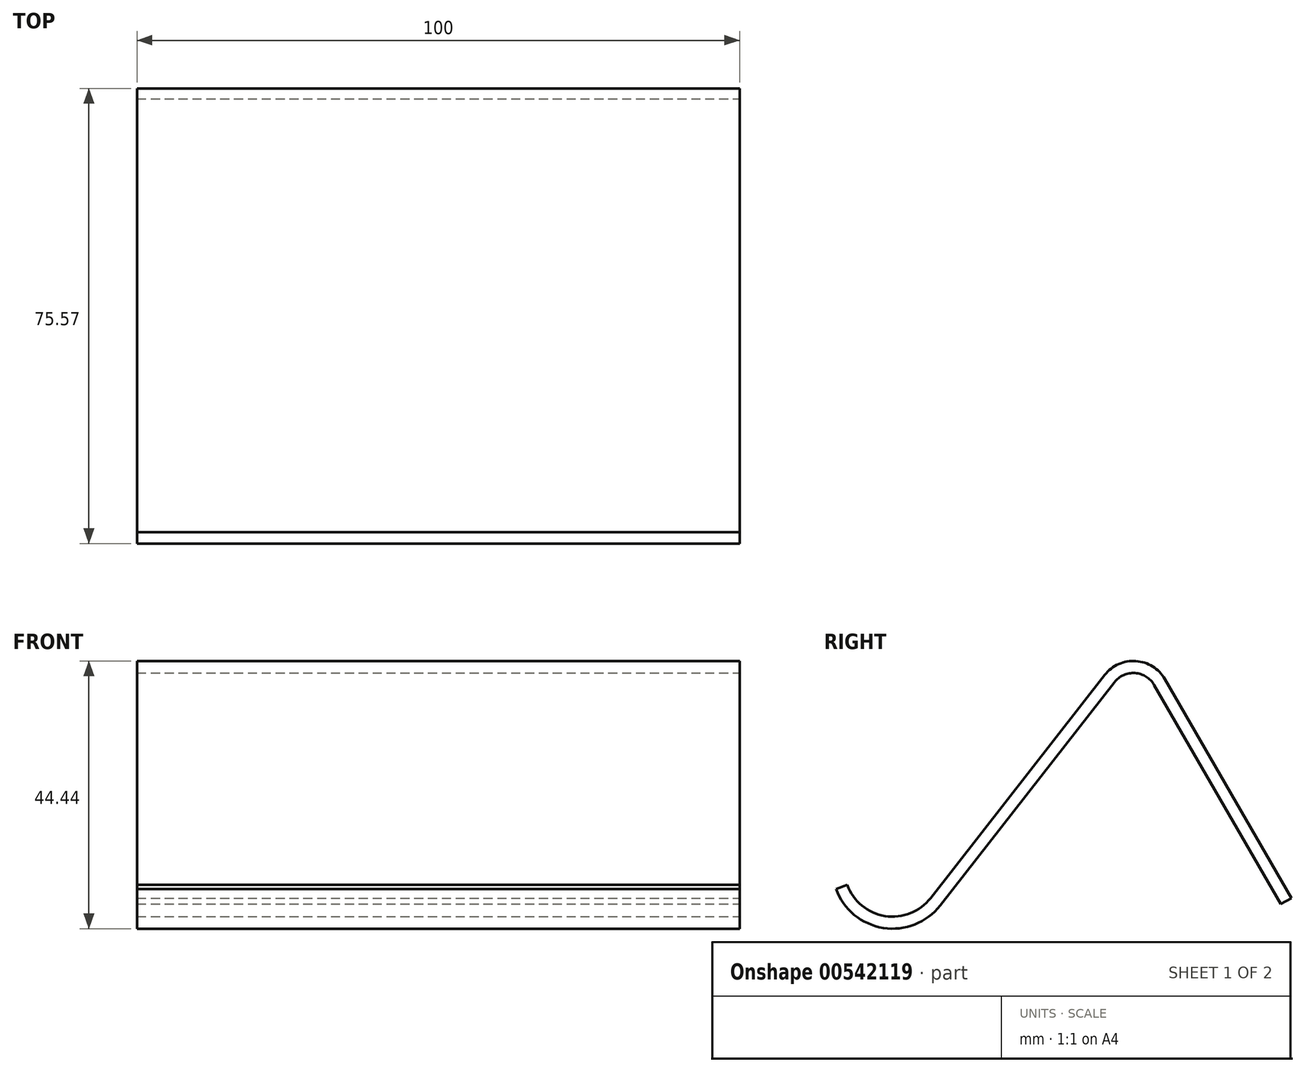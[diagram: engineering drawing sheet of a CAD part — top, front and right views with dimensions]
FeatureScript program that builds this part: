
annotation { "Feature Type Name" : "Feature", "Feature Type Description" : "" }
export const myFeature = defineFeature(function(context is Context, id is Id, definition is map)
    precondition{}
    {
        {
            var Q0;
            Q0=qCreatedBy(makeId("Right.planeOp"),FACE);
            var sketch = newSketch(context, id + "F0", { "sketchPlane" : qUnion([Q0])});
            skLineSegment(sketch, "E0", {"start": v(-34.4, 0) * mm, "end": v(-5.47, 37.05) * mm});
            skLineSegment(sketch, "E1", {"start": v(4.45, 36.36) * mm, "end": v(25.47, 0) * mm});
            skPoint(sketch, "E2.visualSharp", {"position": v(0, 44.06) * mm});
            skArc(sketch, "E2.filletArc", {"start": v(4.45, 36.36) * mm, "mid": v(-0.33, 39.35) * mm, "end": v(-5.47, 37.05) * mm});
            skPoint(sketch, "E3.visualSharp", {"position": v(-34.4, 0) * mm});
            skArc(sketch, "E4", {"start": v(-48.22, 2.2) * mm, "mid": v(-41.95, -2.98) * mm, "end": v(-34.4, 0) * mm});
            skLineSegment(sketch, "E5.0", {"start": v(2.72, 35.36) * mm, "end": v(23.74, -1) * mm});
            skArc(sketch, "E5.1", {"start": v(2.72, 35.36) * mm, "mid": v(-0.47, 37.35) * mm, "end": v(-3.9, 35.82) * mm});
            skLineSegment(sketch, "E5.2", {"start": v(-32.81, -1.23) * mm, "end": v(-3.9, 35.82) * mm});
            skArc(sketch, "E5.3", {"start": v(-50.1, 1.51) * mm, "mid": v(-42.26, -4.95) * mm, "end": v(-32.81, -1.23) * mm});
            skLineSegment(sketch, "E6", {"start": v(-50.1, 1.51) * mm, "end": v(-48.22, 2.2) * mm});
            skLineSegment(sketch, "E7", {"start": v(23.74, -1) * mm, "end": v(25.47, 0) * mm});
            skSolve(sketch);
        }
        {
            var Q0;
            Q0=makeQuery(id+"F0.imprint","IMPRINT",FACE,{"disambiguationData":[TD([[makeQuery(id+"F0.imprint","IMPRINT",EDGE,{"derivedFrom":sQuery(id+"F0.wireOp",EDGE,"E0")}),-1.0]])]});
            extrude(context, id + "F1", {"entities" : qUnion([Q0]), "oppositeDirection" : true, "depth" : 100 * mm, "offsetDistance" : 25 * mm});
        }
    });
